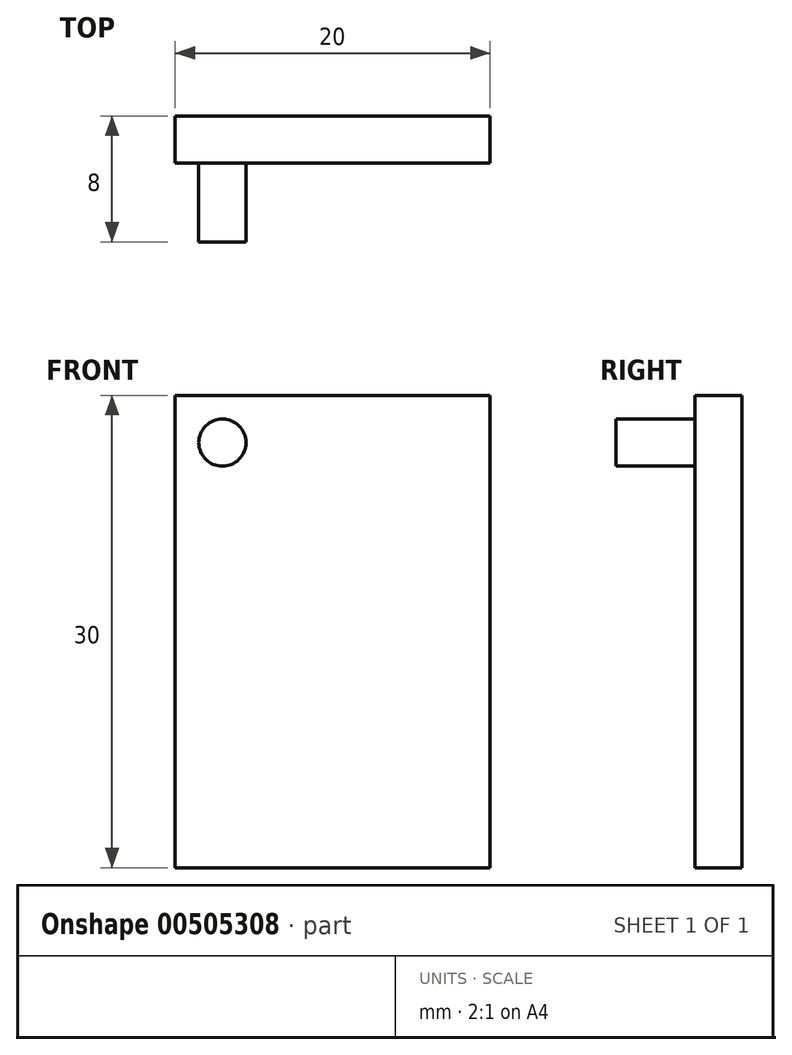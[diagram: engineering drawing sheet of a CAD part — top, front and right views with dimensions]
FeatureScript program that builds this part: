
annotation { "Feature Type Name" : "Feature", "Feature Type Description" : "" }
export const myFeature = defineFeature(function(context is Context, id is Id, definition is map)
    precondition{}
    {
        {
            var Q0;
            Q0=qCreatedBy(makeId("Front.planeOp"),FACE);
            var sketch = newSketch(context, id + "F0", { "sketchPlane" : qUnion([Q0])});
            skLineSegment(sketch, "E0.bottom", {"start": v(-6.7, 3) * mm, "end": v(13.3, 3) * mm});
            skLineSegment(sketch, "E0.top", {"start": v(-6.7, -27) * mm, "end": v(13.3, -27) * mm});
            skLineSegment(sketch, "E0.left", {"start": v(-6.7, 3) * mm, "end": v(-6.7, -27) * mm});
            skLineSegment(sketch, "E0.right", {"start": v(13.3, 3) * mm, "end": v(13.3, -27) * mm});
            skSolve(sketch);
        }
        {
            var Q0;
            Q0=makeQuery(id+"F0.imprint","IMPRINT",FACE,{"disambiguationData":[TD([[makeQuery(id+"F0.imprint","IMPRINT",EDGE,{"derivedFrom":sQuery(id+"F0.wireOp",EDGE,"E0.bottom")}),-1.0]])]});
            var Q1;
            Q1=makeQuery(id+"F0.imprint","IMPRINT",FACE,{"disambiguationData":[TD([[makeQuery(id+"F0.imprint","IMPRINT",EDGE,{"derivedFrom":sQuery(id+"F0.wireOp",EDGE,"pWgONifI-41uo-TG7y-NMao-a4LbJrtrFTWO")}),1.0]])]});
            extrude(context, id + "F1", {"entities" : qUnion([Q0, Q1]), "depth" : 3 * mm});
        }
        {
            var Q0;
            Q0=makeQuery(id+"F1.opExtrude","CAP_FACE",FACE,{"disambiguationData":[OSD([sQuery(id+"F0.wireOp",EDGE,"E0.bottom"),sQuery(id+"F0.wireOp",EDGE,"E0.top"),sQuery(id+"F0.wireOp",EDGE,"E0.left"),sQuery(id+"F0.wireOp",EDGE,"E0.right")])],"isStart":false});
            var sketch = newSketch(context, id + "F2", { "sketchPlane" : qUnion([Q0])});
            skCircle(sketch, "E1", {"center": v(-3.7, 0) * mm, "radius": 1.5 * mm});
            skSolve(sketch);
        }
        {
            var Q0;
            Q0=makeQuery(id+"F2.imprint","IMPRINT",FACE,{"disambiguationData":[TD([[makeQuery(id+"F2.imprint","IMPRINT",EDGE,{"derivedFrom":sQuery(id+"F2.wireOp",EDGE,"E1")}),1.0]])]});
            extrude(context, id + "F3", {"entities" : qUnion([Q0]), "operationType" : NewBodyOperationType.ADD, "depth" : 5 * mm});
        }
    });
